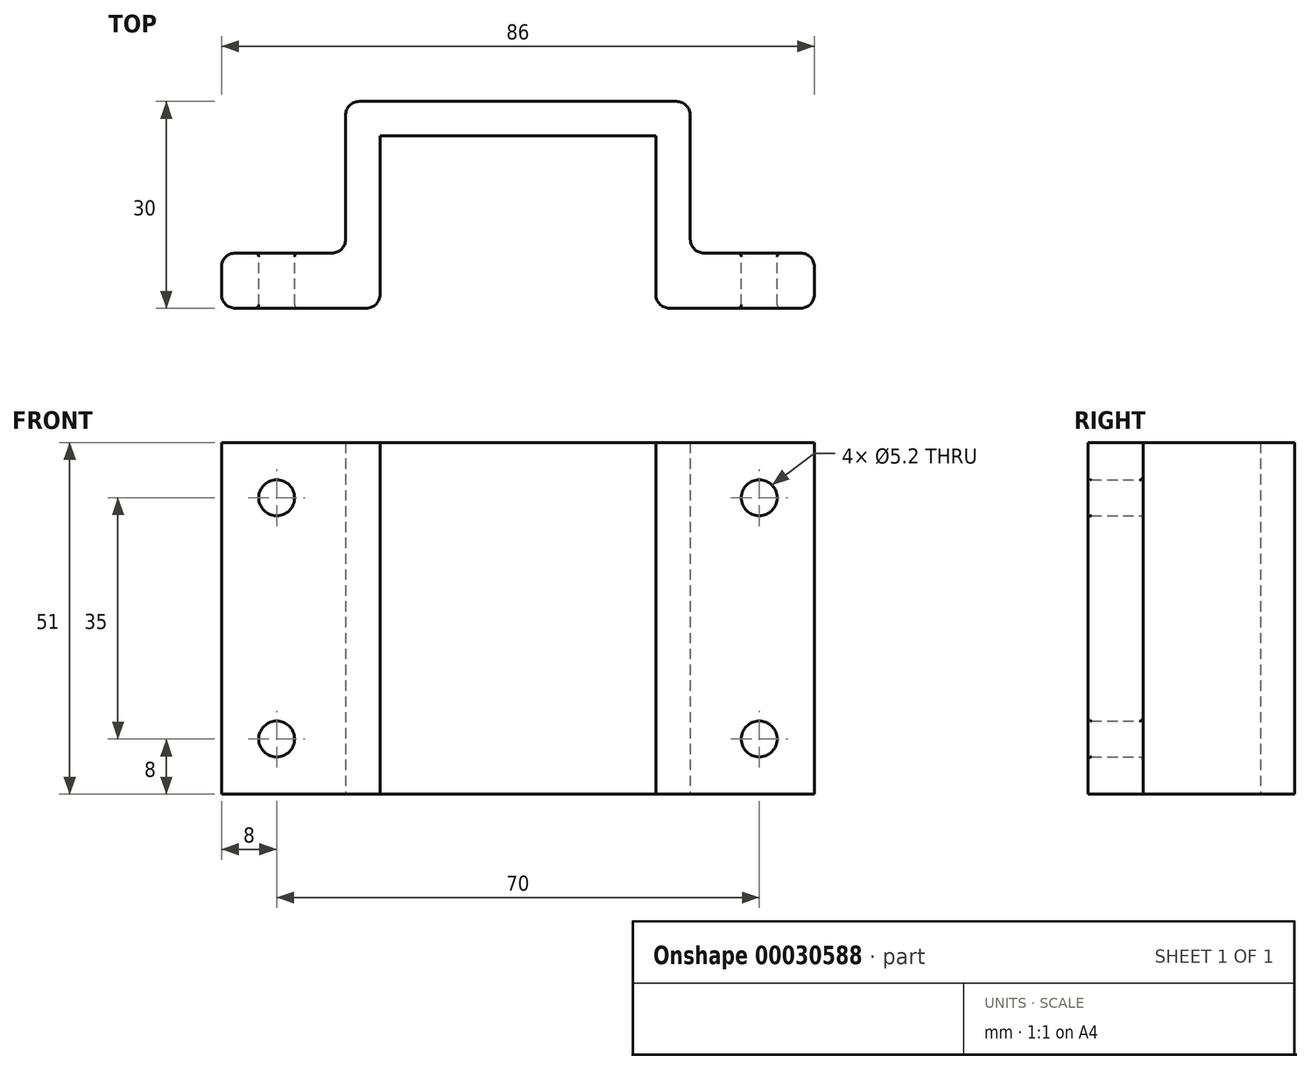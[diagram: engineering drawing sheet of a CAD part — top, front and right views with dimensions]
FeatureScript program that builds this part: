
annotation { "Feature Type Name" : "Feature", "Feature Type Description" : "" }
export const myFeature = defineFeature(function(context is Context, id is Id, definition is map)
    precondition{}
    {
        {
            var Q0;
            Q0=qCreatedBy(makeId("Top.planeOp"),FACE);
            var sketch = newSketch(context, id + "F0", { "sketchPlane" : qUnion([Q0])});
            skLineSegment(sketch, "E0", {"start": v(-20, 0) * mm, "end": v(-20, 25) * mm});
            skLineSegment(sketch, "E1", {"start": v(-20, 25) * mm, "end": v(0, 25) * mm});
            skLineSegment(sketch, "E2", {"start": v(-20, 0) * mm, "end": v(-43, 0) * mm});
            skLineSegment(sketch, "E3", {"start": v(-43, 0) * mm, "end": v(-43, 8) * mm});
            skLineSegment(sketch, "E4", {"start": v(-43, 8) * mm, "end": v(-25, 8) * mm});
            skLineSegment(sketch, "E5", {"start": v(-25, 8) * mm, "end": v(-25, 30) * mm});
            skLineSegment(sketch, "E6", {"start": v(-25, 30) * mm, "end": v(0, 30) * mm});
            skLineSegment(sketch, "E7.MirrorCS", {"start": v(20, 0) * mm, "end": v(20, 25) * mm});
            skLineSegment(sketch, "E8.MirrorCS", {"start": v(20, 25) * mm, "end": v(0, 25) * mm});
            skLineSegment(sketch, "E9.MirrorCS", {"start": v(25, 30) * mm, "end": v(0, 30) * mm});
            skLineSegment(sketch, "E10.MirrorCS", {"start": v(20, 0) * mm, "end": v(43, 0) * mm});
            skLineSegment(sketch, "E11.MirrorCS", {"start": v(43, 0) * mm, "end": v(43, 8) * mm});
            skLineSegment(sketch, "E12.MirrorCS", {"start": v(43, 8) * mm, "end": v(25, 8) * mm});
            skLineSegment(sketch, "E13.MirrorCS", {"start": v(25, 8) * mm, "end": v(25, 30) * mm});
            skSolve(sketch);
        }
        {
            var Q0;
            Q0=makeQuery(id+"F0.imprint","IMPRINT",FACE,{"disambiguationData":[TD([[makeQuery(id+"F0.imprint","IMPRINT",EDGE,{"derivedFrom":sQuery(id+"F0.wireOp",EDGE,"E0")}),1.0]])]});
            extrude(context, id + "F1", {"entities" : qUnion([Q0]), "depth" : 51 * mm});
        }
        {
            var Q0;
            Q0=makeQuery(id+"F1.opExtrude","SWEPT_FACE",FACE,{"disambiguationData":[OSD([sQuery(id+"F0.wireOp",EDGE,"E4")])]});
            var sketch = newSketch(context, id + "F2", { "sketchPlane" : qUnion([Q0])});
            skCircle(sketch, "E14", {"center": v(35, 8) * mm, "radius": 2.6 * mm});
            skCircle(sketch, "E15", {"center": v(35, 43) * mm, "radius": 2.6 * mm});
            skCircle(sketch, "E16", {"center": v(-35, 8) * mm, "radius": 2.6 * mm});
            skCircle(sketch, "E17", {"center": v(-35, 43) * mm, "radius": 2.6 * mm});
            skSolve(sketch);
        }
        {
            var Q0;
            Q0=makeQuery(id+"F1.opExtrude","SWEPT_EDGE",EDGE,{"disambiguationData":[OSD([sQuery(id+"F0.wireOp",EDGE,"E4"),sQuery(id+"F0.wireOp",EDGE,"E5")])]});
            var Q1;
            Q1=makeQuery(id+"F1.opExtrude","SWEPT_EDGE",EDGE,{"disambiguationData":[OSD([sQuery(id+"F0.wireOp",EDGE,"E12.MirrorCS"),sQuery(id+"F0.wireOp",EDGE,"E13.MirrorCS")])]});
            var Q2;
            Q2=makeQuery(id+"F1.opExtrude","SWEPT_EDGE",EDGE,{"disambiguationData":[OSD([sQuery(id+"F0.wireOp",EDGE,"E11.MirrorCS"),sQuery(id+"F0.wireOp",EDGE,"E12.MirrorCS")])]});
            var Q3;
            Q3=makeQuery(id+"F1.opExtrude","SWEPT_EDGE",EDGE,{"disambiguationData":[OSD([sQuery(id+"F0.wireOp",EDGE,"E10.MirrorCS"),sQuery(id+"F0.wireOp",EDGE,"E11.MirrorCS")])]});
            var Q4;
            Q4=makeQuery(id+"F1.opExtrude","SWEPT_EDGE",EDGE,{"disambiguationData":[OSD([sQuery(id+"F0.wireOp",EDGE,"E3"),sQuery(id+"F0.wireOp",EDGE,"E4")])]});
            var Q5;
            Q5=makeQuery(id+"F1.opExtrude","SWEPT_EDGE",EDGE,{"disambiguationData":[OSD([sQuery(id+"F0.wireOp",EDGE,"E2"),sQuery(id+"F0.wireOp",EDGE,"E3")])]});
            var Q6;
            Q6=makeQuery(id+"F1.opExtrude","SWEPT_EDGE",EDGE,{"disambiguationData":[OSD([sQuery(id+"F0.wireOp",EDGE,"E0"),sQuery(id+"F0.wireOp",EDGE,"E2")])]});
            var Q7;
            Q7=makeQuery(id+"F1.opExtrude","SWEPT_EDGE",EDGE,{"disambiguationData":[OSD([sQuery(id+"F0.wireOp",EDGE,"E7.MirrorCS"),sQuery(id+"F0.wireOp",EDGE,"E10.MirrorCS")])]});
            var Q8;
            Q8=makeQuery(id+"F1.opExtrude","SWEPT_EDGE",EDGE,{"disambiguationData":[OSD([sQuery(id+"F0.wireOp",EDGE,"E5"),sQuery(id+"F0.wireOp",EDGE,"E6")])]});
            var Q9;
            Q9=makeQuery(id+"F1.opExtrude","SWEPT_EDGE",EDGE,{"disambiguationData":[OSD([sQuery(id+"F0.wireOp",EDGE,"E9.MirrorCS"),sQuery(id+"F0.wireOp",EDGE,"E13.MirrorCS")])]});
            fillet(context, id + "F3", {"entities" : qUnion([Q0, Q1, Q2, Q3, Q4, Q5, Q6, Q7, Q8, Q9]), "radius" : 2 * mm, "tangentPropagation" : true, "allowEdgeOverflow" : false});
        }
        {
            var Q0;
            Q0 = qSketchRegion(id + "F2", true);
            var Q1;
            Q1=makeQuery(id+"F1.opExtrude","SWEPT_FACE",FACE,{"disambiguationData":[OSD([sQuery(id+"F0.wireOp",EDGE,"E2")])]});
            extrude(context, id + "F4", {"entities" : qUnion([Q0]), "operationType" : NewBodyOperationType.REMOVE, "endBound" : BoundingType.UP_TO_SURFACE, "oppositeDirection" : true, "endBoundEntityFace" : qUnion([Q1]), "depth" : 25 * mm});
        }
        {
            var Q0;
            Q0=makeQuery(id+"F4.boolean.opBoolean","COPY",FACE,{"derivedFrom":makeQuery(id+"F4.opExtrude","SWEPT_FACE",FACE,{"disambiguationData":[OSD([sQuery(id+"F2.wireOp",EDGE,"E15")])]})});
            var Q1;
            Q1=makeQuery(id+"F4.boolean.opBoolean","COPY",FACE,{"derivedFrom":makeQuery(id+"F4.opExtrude","SWEPT_FACE",FACE,{"disambiguationData":[OSD([sQuery(id+"F2.wireOp",EDGE,"E14")])]})});
            var Q2;
            Q2=makeQuery(id+"F4.boolean.opBoolean","COPY",FACE,{"derivedFrom":makeQuery(id+"F4.opExtrude","SWEPT_FACE",FACE,{"disambiguationData":[OSD([sQuery(id+"F2.wireOp",EDGE,"E16")])]})});
            var Q3;
            Q3=makeQuery(id+"F4.boolean.opBoolean","COPY",FACE,{"derivedFrom":makeQuery(id+"F4.opExtrude","SWEPT_FACE",FACE,{"disambiguationData":[OSD([sQuery(id+"F2.wireOp",EDGE,"E17")])]})});
            fillet(context, id + "F5", {"entities" : qUnion([Q0, Q1, Q2, Q3]), "radius" : 0.5 * mm, "tangentPropagation" : true, "allowEdgeOverflow" : false});
        }
    });
